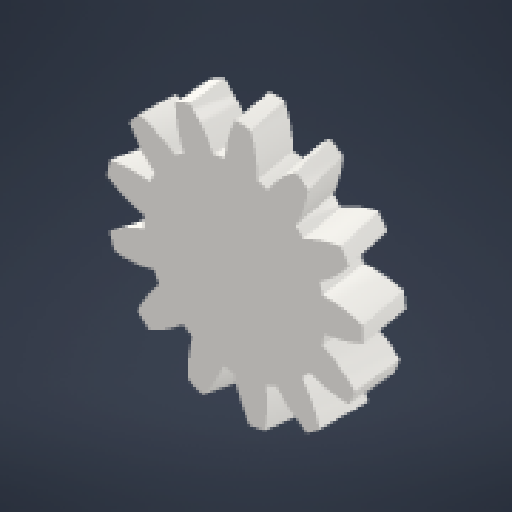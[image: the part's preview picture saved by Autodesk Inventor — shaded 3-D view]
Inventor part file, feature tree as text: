
AUTODESK INVENTOR PART (.ipt)
format: ipt  version: 2024.2 (Build 282272000, 272)  size: 384,000 bytes
history: native  units: mm (DEFAULTED — no unit token found)
features: other x6, extrude x4, sketch x4, plane x3
ambient origin geometry x8: Origin, YZ Plane, XZ Plane, XY Plane, X Axis, Y Axis, Z Axis, Center Point
bodies: Solid1 (feature_tree)
feature tree (17):
  extrude  "Extrusion1"  Depth=6.35mm TaperAngle=0.0deg
  plane  "Work Plane1"
  plane  "Work Plane2"
  plane  "Work Plane3"
  other  "Spur Gear"
  extrude  "Extrusion4"  Depth=76.2mm TaperAngle=0.0deg
  extrude  "Extrusion5"  TaperAngle=0.0deg  [1 undecoded]
  other  "Work Point1"
  other  "Work Point2"
  other  "Work Axis1"
  extrude  "Extrusion6"  Depth=1.0mm
  sketch  "Sketch1"  dims[d0=38.570605mm d1=6.35mm d2=0.0mm]
  other  "Srf1"
  sketch  "Sketch5"  dims[d3=33.529387mm d4=76.2mm d5=0.0mm]
  sketch  "Sketch6"  dims[d6=0.0mm d7=2.41661mm d9=0.0mm]
  sketch  "Sketch7"  dims[d14=0.0mm d15=35.513307mm d16=0.0mm d17=0.0mm d18=0.0mm d19=35.513307mm d26=15.0mm d27=1.0mm d28=0.0mm d29=14.0mm d30=0.0mm d31=0.0mm d32=4.0mm d33=4.0mm d34=4.0mm d35=4.0mm d36=0.0mm d37=0.0mm]
  other  "Pitch Diameter"
note: 1 required parameter value undecoded (feature->parameter linkage not recoverable at this tier; creation-order binding heuristic only, values carry confidence <= 0.55)
